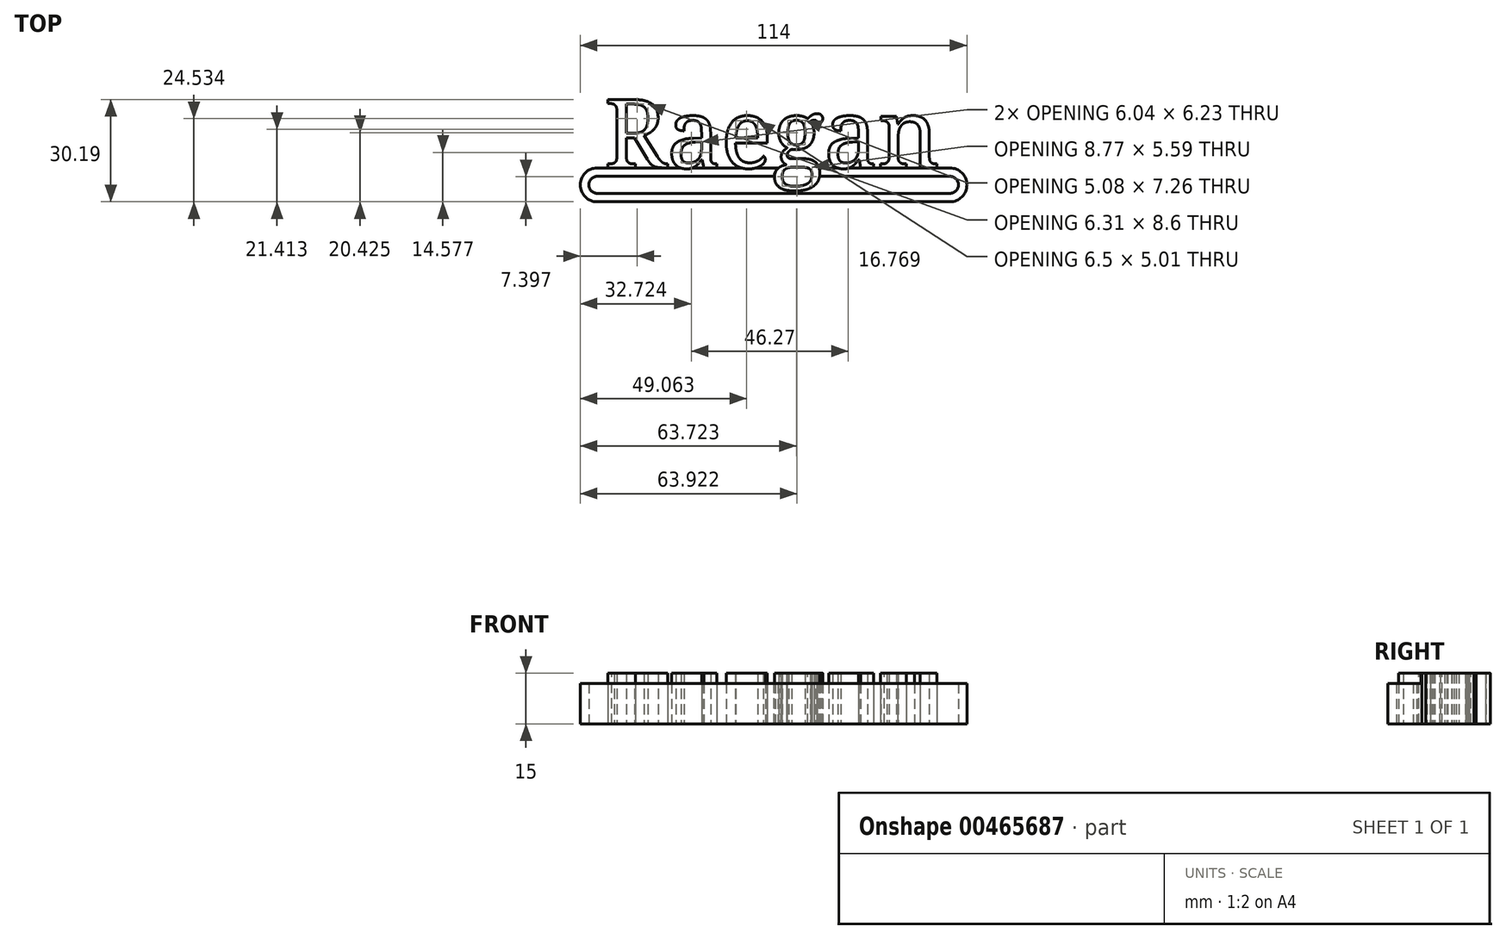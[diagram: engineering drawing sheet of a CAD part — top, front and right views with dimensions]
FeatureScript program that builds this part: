
annotation { "Feature Type Name" : "Feature", "Feature Type Description" : "" }
export const myFeature = defineFeature(function(context is Context, id is Id, definition is map)
    precondition{}
    {
        {
            var Q0;
            Q0=qCreatedBy(makeId("Top.planeOp"),FACE);
            var sketch = newSketch(context, id + "F0", { "sketchPlane" : qUnion([Q0])});
            skText(sketch, "E0", { "text": "Raegan", "fontName": "NotoSerif-Regular.ttf"});
            const initialGuessF0  = {"E0": [-0.05, 0, 1, 0, 0.02036]};
            skSetInitialGuess(sketch, initialGuessF0);
            skSolve(sketch);
        }
        {
            var Q0;
            Q0 = qSketchRegion(id + "F0", true);
            extrude(context, id + "F1", {"entities" : qUnion([Q0]), "depth" : 15 * mm});
        }
        {
            var Q0;
            Q0=qCreatedBy(makeId("Top.planeOp"),FACE);
            var sketch = newSketch(context, id + "F2", { "sketchPlane" : qUnion([Q0])});
            skLineSegment(sketch, "E1", {"start": v(0, 0) * mm, "end": v(-52, 0) * mm});
            skLineSegment(sketch, "E2", {"start": v(-52, -5) * mm, "end": v(-52, -5) * mm});
            skLineSegment(sketch, "E3", {"start": v(-52, -10) * mm, "end": v(0, -10) * mm});
            skLineSegment(sketch, "E4", {"start": v(0, -7.5) * mm, "end": v(-52, -7.5) * mm});
            skLineSegment(sketch, "E5", {"start": v(0, -2.5) * mm, "end": v(-52, -2.5) * mm});
            skArc(sketch, "E6", {"start": v(-52, 0) * mm, "mid": v(-57, -5) * mm, "end": v(-52, -10) * mm});
            skArc(sketch, "E7", {"start": v(-52, -2.5) * mm, "mid": v(-54.5, -5) * mm, "end": v(-52, -7.5) * mm});
            skLineSegment(sketch, "E8", {"start": v(0, 7.88) * mm, "end": v(0, -18.45) * mm, "construction": true});
            skArc(sketch, "E9.MirrorCS", {"start": v(52, -2.5) * mm, "mid": v(54.5, -5) * mm, "end": v(52, -7.5) * mm});
            skArc(sketch, "E10.MirrorCS", {"start": v(52, 0) * mm, "mid": v(57, -5) * mm, "end": v(52, -10) * mm});
            skLineSegment(sketch, "E11.MirrorCS", {"start": v(0, 0) * mm, "end": v(1.48, 0) * mm});
            skLineSegment(sketch, "E12.MirrorCS", {"start": v(0, -2.5) * mm, "end": v(0.24, -2.5) * mm});
            skLineSegment(sketch, "E13.MirrorCS", {"start": v(0, -7.5) * mm, "end": v(52, -7.5) * mm});
            skLineSegment(sketch, "E14.MirrorCS", {"start": v(52, -10) * mm, "end": v(0, -10) * mm});
            skFitSpline(sketch, "E15.0.27", {"points": [v(2.43, 0.57) * mm, v(1.8, 0.3) * mm, v(1.3, -0.15) * mm]});
            skFitSpline(sketch, "E15.0.28", {"points": [v(1.3, -0.15) * mm, v(0.82, -0.6) * mm, v(0.53, -1.21) * mm]});
            skFitSpline(sketch, "E15.0.29", {"points": [v(0.53, -1.21) * mm, v(0.24, -1.84) * mm, v(0.24, -2.66) * mm]});
            skFitSpline(sketch, "E15.0.35", {"points": [v(13.16, -3.7) * mm, v(13.61, -2.72) * mm, v(13.61, -1.5) * mm]});
            skFitSpline(sketch, "E15.0.36", {"points": [v(13.61, -1.5) * mm, v(13.61, -0.6) * mm, v(13.36, 0.19) * mm]});
            skLineSegment(sketch, "E16.trimOffspring", {"start": v(13.53, -2.5) * mm, "end": v(52, -2.5) * mm});
            skLineSegment(sketch, "E17.trimOffspring", {"start": v(13.41, 0) * mm, "end": v(52, 0) * mm});
            skSolve(sketch);
        }
        {
            var Q0;
            Q0=makeQuery(id+"F2.imprint","IMPRINT",FACE,{"disambiguationData":[TD([[makeQuery(id+"F2.imprint","IMPRINT",EDGE,{"derivedFrom":sQuery(id+"F2.wireOp",EDGE,"E1")}),1.0]])]});
            extrude(context, id + "F3", {"entities" : qUnion([Q0]), "depth" : 12 * mm});
        }
    });
